annotation { "Feature Type Name" : "Feature", "Feature Type Description" : "" }
export const myFeature = defineFeature(function(context is Context, id is Id, definition is map)
    precondition{}
    {
        {
            var Q0;
            Q0=qCreatedBy(makeId("Front.planeOp"),FACE);
            var sketch = newSketch(context, id + "F0", { "sketchPlane" : qUnion([Q0])});
            skLineSegment(sketch, "E0.bottom", {"start": v(-38.96, 47.22) * mm, "end": v(37.24, 47.22) * mm});
            skLineSegment(sketch, "E0.top", {"start": v(-38.96, -67.08) * mm, "end": v(37.24, -67.08) * mm});
            skLineSegment(sketch, "E0.left", {"start": v(-38.96, 47.22) * mm, "end": v(-38.96, -67.08) * mm});
            skLineSegment(sketch, "E0.right", {"start": v(37.24, 47.22) * mm, "end": v(37.24, -67.08) * mm});
            skSolve(sketch);
        }
        {
            var Q0;
            Q0 = qSketchRegion(id + "F0", true);
            extrude(context, id + "F1", {"entities" : qUnion([Q0]), "depth" : 3.17 * mm});
        }
        {
            var Q0;
            Q0=qCreatedBy(makeId("Front.planeOp"),FACE);
            var sketch = newSketch(context, id + "F2", { "sketchPlane" : qUnion([Q0])});
            skText(sketch, "E1", { "text": "Hall Pass", "fontName": "RobotoSlab-Bold.ttf"});
            const initialGuessF2  = {"E1": [-0.03676, 0.0283, 1, 0, 0.01146]};
            skSetInitialGuess(sketch, initialGuessF2);
            skSolve(sketch);
        }
        {
            var Q0;
            Q0 = qSketchRegion(id + "F2", true);
            extrude(context, id + "F3", {"entities" : qUnion([Q0]), "operationType" : NewBodyOperationType.ADD, "depth" : 6.35 * mm});
        }
        {
            var Q0;
            Q0=qCreatedBy(makeId("Front.planeOp"),FACE);
            var sketch = newSketch(context, id + "F4", { "sketchPlane" : qUnion([Q0])});
            skFitSpline(sketch, "E2", {"points": [v(-20.06, 4.67) * mm, v(-17.14, 9.5) * mm, v(-14.6, 13.55) * mm, v(-11.69, 16.85) * mm, v(-6.49, 16.6) * mm, v(-2.68, 12.92) * mm, v(-1.16, 10.25) * mm], "startDerivative": vector(16.2, 27.06) * mm, "endDerivative": vector(9.6, -18.67) * mm});
            skFitSpline(sketch, "E3", {"points": [v(-20.06, 4.67) * mm, v(-8.26, -2.43) * mm], "startDerivative": vector(11.8, -7.1) * mm, "endDerivative": vector(11.8, -7.1) * mm});
            skFitSpline(sketch, "E4", {"points": [v(-1.16, 10.25) * mm, v(-8.26, -2.43) * mm], "startDerivative": vector(-7.1, -12.68) * mm, "endDerivative": vector(-7.1, -12.68) * mm});
            skFitSpline(sketch, "E5", {"points": [v(-29.55, -2.43) * mm, v(-16.13, -2.43) * mm], "startDerivative": vector(13.29, 0) * mm, "endDerivative": vector(13.29, 0) * mm});
            skFitSpline(sketch, "E6", {"points": [v(-16.13, -2.43) * mm, v(-9.91, -13.34) * mm], "startDerivative": vector(6.21, -10.9) * mm, "endDerivative": vector(6.21, -10.9) * mm});
            skFitSpline(sketch, "E7", {"points": [v(-9.91, -13.34) * mm, v(-13.33, -11.56) * mm], "startDerivative": vector(-3.42, 1.78) * mm, "endDerivative": vector(-3.42, 1.78) * mm});
            skFitSpline(sketch, "E8", {"points": [v(-13.33, -11.56) * mm, v(-19.93, -22.22) * mm], "startDerivative": vector(-6.6, -10.65) * mm, "endDerivative": vector(-6.6, -10.65) * mm});
            skFitSpline(sketch, "E9", {"points": [v(-19.93, -22.22) * mm, v(-21.2, -24.63) * mm, v(-21.33, -27.42) * mm, v(-21.45, -27.42) * mm], "startDerivative": vector(-3.65, -4.46) * mm, "endDerivative": vector(-1.47, 0.62) * mm});
            skFitSpline(sketch, "E10", {"points": [v(-21.33, -27.42) * mm, v(-28.05, -16) * mm, v(-28.03, -16.03) * mm], "startDerivative": vector(-10.64, 17.96) * mm, "endDerivative": vector(0.64, -0.84) * mm});
            skFitSpline(sketch, "E11", {"points": [v(-28.03, -16.03) * mm, v(-29.55, -13.77) * mm, v(-29.55, -12.36) * mm, v(-28.03, -9.7) * mm, v(-25.25, -4.96) * mm], "startDerivative": vector(-7.33, 10.07) * mm, "endDerivative": vector(8.56, 14.74) * mm});
            skFitSpline(sketch, "E12", {"points": [v(-29.55, -2.43) * mm, v(-25.25, -4.96) * mm], "startDerivative": vector(4.16, -2.53) * mm, "endDerivative": vector(4.16, -2.53) * mm});
            skFitSpline(sketch, "E13", {"points": [v(-16.92, -20.04) * mm, v(-2.28, -20.12) * mm], "startDerivative": vector(14.65, -0.09) * mm, "endDerivative": vector(14.65, -0.09) * mm});
            skFitSpline(sketch, "E14", {"points": [v(-2.28, -20.12) * mm, v(-2.28, -33.36) * mm], "startDerivative": vector(0, -13.23) * mm, "endDerivative": vector(0, -13.23) * mm});
            skFitSpline(sketch, "E15", {"points": [v(-2.28, -33.36) * mm, v(-13.33, -33.36) * mm, v(-14.6, -33.36) * mm, v(-17, -32.56) * mm, v(-19.04, -30.45) * mm, v(-19.93, -26.56) * mm, v(-16.92, -20.04) * mm], "startDerivative": vector(-52.33, 0.37) * mm, "endDerivative": vector(19.26, 31.54) * mm});
            skFitSpline(sketch, "E16", {"points": [v(21.55, 0.61) * mm, v(27.05, -8.9) * mm], "startDerivative": vector(5.5, -9.52) * mm, "endDerivative": vector(5.5, -9.52) * mm});
            skFitSpline(sketch, "E17", {"points": [v(27.05, -8.9) * mm, v(27.9, -10.91) * mm, v(27.9, -13.03) * mm, v(27.05, -15.14) * mm, v(26.36, -16.15) * mm, v(24.67, -17.63) * mm, v(23.19, -18.26) * mm], "startDerivative": vector(6.57, -11.02) * mm, "endDerivative": vector(-9.48, -3.04) * mm});
            skFitSpline(sketch, "E18", {"points": [v(23.19, -18.26) * mm, v(21.5, -18.58) * mm, v(17.32, -18.69) * mm], "startDerivative": vector(-3.83, -0.94) * mm, "endDerivative": vector(-7.63, 0.02) * mm});
            skFitSpline(sketch, "E19", {"points": [v(17.32, -18.69) * mm, v(10.02, -6.26) * mm], "startDerivative": vector(-7.3, 12.42) * mm, "endDerivative": vector(-7.3, 12.42) * mm});
            skFitSpline(sketch, "E20", {"points": [v(10.02, -6.26) * mm, v(21.6, 0.61) * mm], "startDerivative": vector(11.58, 6.87) * mm, "endDerivative": vector(11.58, 6.87) * mm});
            skFitSpline(sketch, "E21", {"points": [v(10.09, 17.82) * mm, v(-5.43, 17.82) * mm], "startDerivative": vector(-15.52, 0) * mm, "endDerivative": vector(-15.52, 0) * mm});
            skFitSpline(sketch, "E22", {"points": [v(10.09, 17.82) * mm, v(11.26, 17.53) * mm, v(12.33, 16.6) * mm, v(13.56, 14.55) * mm, v(15.19, 11.86) * mm, v(16.29, 10) * mm, v(16.35, 9.97) * mm], "startDerivative": vector(8.11, -1.26) * mm, "endDerivative": vector(1.48, -0.2) * mm});
            skFitSpline(sketch, "E23", {"points": [v(16.35, 9.97) * mm, v(20.28, 12.28) * mm], "startDerivative": vector(3.93, 2.3) * mm, "endDerivative": vector(3.93, 2.3) * mm});
            skFitSpline(sketch, "E24", {"points": [v(20.28, 12.28) * mm, v(14, 0.7) * mm], "startDerivative": vector(-6.28, -11.58) * mm, "endDerivative": vector(-6.28, -11.58) * mm});
            skFitSpline(sketch, "E25", {"points": [v(14, 0.7) * mm, v(0.43, 0.78) * mm], "startDerivative": vector(-13.56, 0.08) * mm, "endDerivative": vector(-13.56, 0.08) * mm});
            skFitSpline(sketch, "E26", {"points": [v(0.43, 0.78) * mm, v(4.32, 2.93) * mm], "startDerivative": vector(3.89, 2.15) * mm, "endDerivative": vector(3.89, 2.15) * mm});
            skFitSpline(sketch, "E27", {"points": [v(4.32, 2.93) * mm, v(-1.72, 14.1) * mm, v(-2.68, 15.83) * mm, v(-3.78, 16.6) * mm, v(-5.43, 17.82) * mm], "startDerivative": vector(-15.86, 28.57) * mm, "endDerivative": vector(-8.9, 7.13) * mm});
            skFitSpline(sketch, "E28", {"points": [v(8, -15.4) * mm, v(8.07, -20.01) * mm], "startDerivative": vector(0.07, -4.61) * mm, "endDerivative": vector(0.07, -4.61) * mm});
            skFitSpline(sketch, "E29", {"points": [v(8.07, -20.01) * mm, v(20.4, -20.01) * mm], "startDerivative": vector(12.33, 0) * mm, "endDerivative": vector(12.33, 0) * mm});
            skFitSpline(sketch, "E30", {"points": [v(20.4, -20.01) * mm, v(22.64, -20.01) * mm, v(24.58, -19.15) * mm, v(25.74, -18.71) * mm], "startDerivative": vector(6.16, -0.72) * mm, "endDerivative": vector(3.98, 1.25) * mm});
            skFitSpline(sketch, "E31", {"points": [v(25.74, -18.71) * mm, v(18.46, -31.62) * mm], "startDerivative": vector(-7.28, -12.9) * mm, "endDerivative": vector(-7.28, -12.9) * mm});
            skFitSpline(sketch, "E32", {"points": [v(18.46, -31.62) * mm, v(17.6, -32.77) * mm, v(16.5, -33.42) * mm, v(8.07, -33.7) * mm], "startDerivative": vector(-3.8, -5.46) * mm, "endDerivative": vector(-18.85, 0.23) * mm});
            skFitSpline(sketch, "E33", {"points": [v(8.07, -33.7) * mm, v(8, -38.03) * mm], "startDerivative": vector(-0.07, -4.33) * mm, "endDerivative": vector(-0.07, -4.33) * mm});
            skFitSpline(sketch, "E34", {"points": [v(8, -38.03) * mm, v(1.23, -26.79) * mm], "startDerivative": vector(-6.78, 11.25) * mm, "endDerivative": vector(-6.78, 11.25) * mm});
            skFitSpline(sketch, "E35", {"points": [v(1.23, -26.79) * mm, v(8, -15.4) * mm], "startDerivative": vector(6.78, 11.4) * mm, "endDerivative": vector(6.78, 11.4) * mm});
            skSolve(sketch);
        }
        {
            var Q0;
            {var subQ0=sQuery(id+"F0.wireOp",EDGE,"E0.top");var subQ1=sQuery(id+"F0.wireOp",EDGE,"E0.right");var subQ2=sQuery(id+"F0.wireOp",EDGE,"E0.bottom");var subQ3=sQuery(id+"F0.wireOp",EDGE,"E0.left");Q0=makeQuery(id+"F3.boolean.opBoolean","SPLIT",FACE,{"disambiguationData":[TD([makeQuery(id+"F1.opExtrude","SWEPT_FACE",FACE,{"disambiguationData":[OSD([subQ2])]})])],"derivedFrom":makeQuery(id+"F1.opExtrude","CAP_FACE",FACE,{"disambiguationData":[OSD([subQ2,subQ0,subQ3,subQ1])],"isStart":false})});}
            var sketch = newSketch(context, id + "F5", { "sketchPlane" : qUnion([Q0])});
            skText(sketch, "E36", { "text": "S.T.E.M.", "fontName": "RobotoSlab-Bold.ttf"});
            const initialGuessF5  = {"E36": [-0.03827, -0.05868, 1, 0, 0.0141]};
            skSetInitialGuess(sketch, initialGuessF5);
            skSolve(sketch);
        }
        {
            var Q0;
            Q0 = qSketchRegion(id + "F5", true);
            extrude(context, id + "F6", {"entities" : qUnion([Q0]), "operationType" : NewBodyOperationType.REMOVE, "oppositeDirection" : true, "depth" : 25.4 * mm});
        }
        {
            var Q0;
            Q0 = qSketchRegion(id + "F4", true);
            extrude(context, id + "F7", {"entities" : qUnion([Q0]), "operationType" : NewBodyOperationType.ADD, "depth" : 6.35 * mm});
        }
        {
            var Q0;
            {var subQ0=sQuery(id+"F0.wireOp",EDGE,"E0.top");var subQ1=sQuery(id+"F0.wireOp",EDGE,"E0.right");var subQ2=sQuery(id+"F0.wireOp",EDGE,"E0.bottom");var subQ3=sQuery(id+"F0.wireOp",EDGE,"E0.left");Q0=makeQuery(id+"F3.boolean.opBoolean","SPLIT",FACE,{"disambiguationData":[TD([makeQuery(id+"F1.opExtrude","SWEPT_FACE",FACE,{"disambiguationData":[OSD([subQ2])]})])],"derivedFrom":makeQuery(id+"F1.opExtrude","CAP_FACE",FACE,{"disambiguationData":[OSD([subQ2,subQ0,subQ3,subQ1])],"isStart":false})});}
            var sketch = newSketch(context, id + "F8", { "sketchPlane" : qUnion([Q0])});
            skCircle(sketch, "E37", {"center": v(0, 68.76) * mm, "radius": 3.18 * mm});
            skCircle(sketch, "E38", {"center": v(0, 43.3) * mm, "radius": 3.18 * mm});
            skSolve(sketch);
        }
        {
            var Q0;
            Q0 = qSketchRegion(id + "F8", true);
            extrude(context, id + "F9", {"entities" : qUnion([Q0]), "operationType" : NewBodyOperationType.REMOVE, "oppositeDirection" : true, "depth" : 3.17 * mm});
        }
    });